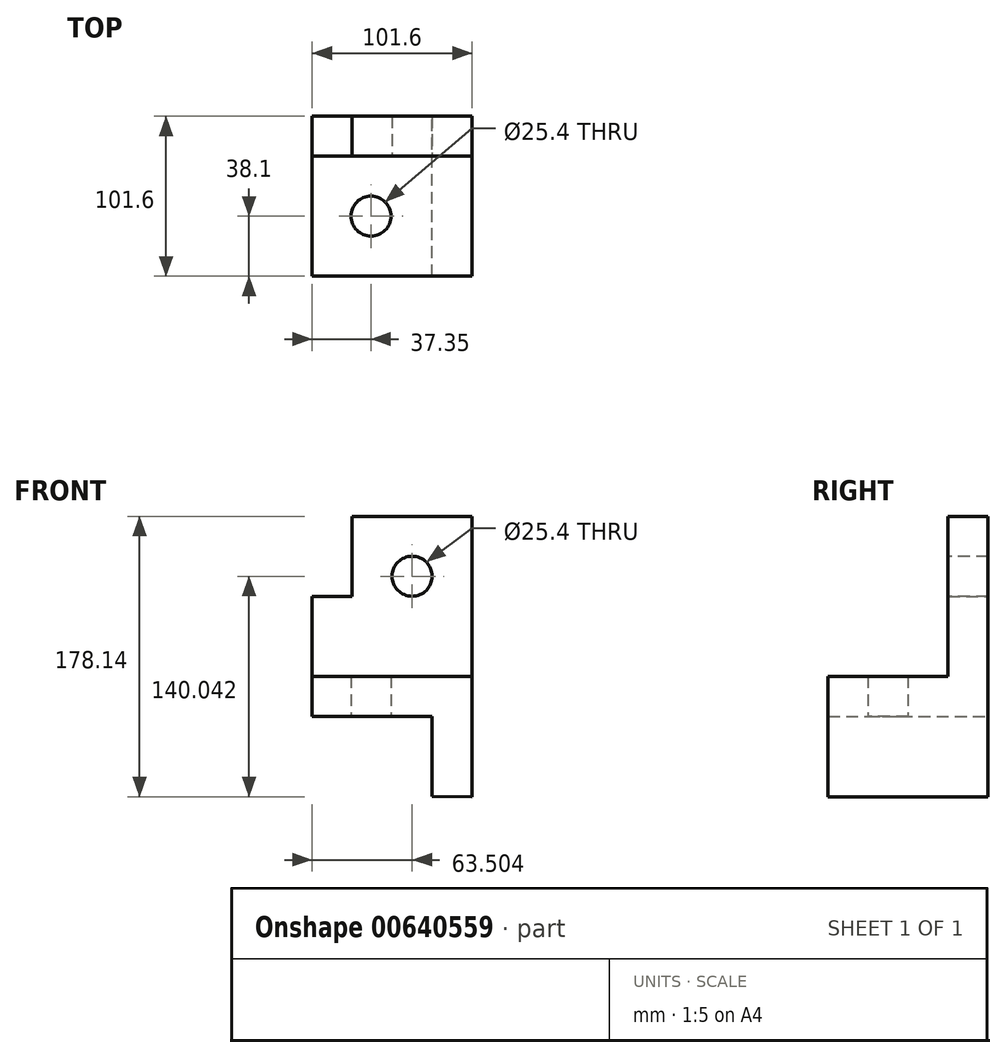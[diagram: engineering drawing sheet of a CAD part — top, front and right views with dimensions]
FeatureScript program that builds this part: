
annotation { "Feature Type Name" : "Feature", "Feature Type Description" : "" }
export const myFeature = defineFeature(function(context is Context, id is Id, definition is map)
    precondition{}
    {
        {
            var Q0;
            Q0=qCreatedBy(makeId("Front.planeOp"),FACE);
            var sketch = newSketch(context, id + "F0", { "sketchPlane" : qUnion([Q0])});
            skLineSegment(sketch, "E0", {"start": v(-11.95, 80.41) * mm, "end": v(64.25, 80.41) * mm});
            skLineSegment(sketch, "E1", {"start": v(64.25, 80.41) * mm, "end": v(64.25, -97.73) * mm});
            skLineSegment(sketch, "E2", {"start": v(-37.35, 29.61) * mm, "end": v(-11.95, 29.61) * mm});
            skLineSegment(sketch, "E3", {"start": v(-11.95, 80.41) * mm, "end": v(-11.95, 29.61) * mm});
            skLineSegment(sketch, "E4", {"start": v(-37.35, -46.59) * mm, "end": v(38.86, -46.59) * mm});
            skLineSegment(sketch, "E5", {"start": v(38.86, -46.59) * mm, "end": v(38.86, -97.39) * mm});
            skLineSegment(sketch, "E6", {"start": v(38.86, -97.39) * mm, "end": v(64.25, -97.73) * mm});
            skPoint(sketch, "E7", {"position": v(-37.35, -46.59) * mm});
            skLineSegment(sketch, "E8", {"start": v(-37.35, 29.61) * mm, "end": v(-37.35, -46.59) * mm});
            skLineSegment(sketch, "E9", {"start": v(-37.35, -21.19) * mm, "end": v(64.25, -21.19) * mm});
            skSolve(sketch);
        }
        {
            var Q0;
            {var subQ2=sQuery(id+"F0.wireOp",EDGE,"E0");Q0=makeQuery(id+"F0.imprint","IMPRINT",FACE,{"disambiguationData":[TD([[makeQuery(id+"F0.imprint","IMPRINT",EDGE,{"derivedFrom":subQ2}),-1.0]])]});}
            extrude(context, id + "F1", {"entities" : qUnion([Q0]), "depth" : 25.4 * mm, "offsetDistance" : 25.4 * mm});
        }
        {
            var Q0;
            {var subQ0=sQuery(id+"F0.wireOp",EDGE,"E4");Q0=makeQuery(id+"F0.imprint","IMPRINT",FACE,{"disambiguationData":[TD([[makeQuery(id+"F0.imprint","IMPRINT",EDGE,{"derivedFrom":subQ0}),1.0]])]});}
            extrude(context, id + "F2", {"entities" : qUnion([Q0]), "operationType" : NewBodyOperationType.ADD, "depth" : 101.6 * mm, "offsetDistance" : 25.4 * mm});
        }
        {
            var Q0;
            Q0=makeQuery(id+"F1.opExtrude","CAP_FACE",FACE,{"disambiguationData":[OSD([sQuery(id+"F0.wireOp",EDGE,"E0"),sQuery(id+"F0.wireOp",EDGE,"E1"),sQuery(id+"F0.wireOp",EDGE,"E2"),sQuery(id+"F0.wireOp",EDGE,"E3"),sQuery(id+"F0.wireOp",EDGE,"E8"),sQuery(id+"F0.wireOp",EDGE,"E9")])],"isStart":false});
            var sketch = newSketch(context, id + "F3", { "sketchPlane" : qUnion([Q0])});
            skCircle(sketch, "E10", {"center": v(26.15, 42.31) * mm, "radius": 12.7 * mm});
            skSolve(sketch);
        }
        {
            var Q0;
            Q0=makeQuery(id+"F3.imprint","IMPRINT",FACE,{"disambiguationData":[TD([[makeQuery(id+"F3.imprint","IMPRINT",EDGE,{"derivedFrom":sQuery(id+"F3.wireOp",EDGE,"E10")}),1.0]])]});
            extrude(context, id + "F4", {"entities" : qUnion([Q0]), "operationType" : NewBodyOperationType.REMOVE, "oppositeDirection" : true, "depth" : 25.4 * mm, "offsetDistance" : 25.4 * mm});
        }
        {
            var Q0;
            Q0=makeQuery(id+"F2.opExtrude","SWEPT_FACE",FACE,{"disambiguationData":[OSD([sQuery(id+"F0.wireOp",EDGE,"E4")])]});
            var sketch = newSketch(context, id + "F5", { "sketchPlane" : qUnion([Q0])});
            skCircle(sketch, "E11", {"center": v(0, 63.5) * mm, "radius": 12.7 * mm});
            skSolve(sketch);
        }
        {
            var Q0;
            Q0=makeQuery(id+"F5.imprint","IMPRINT",FACE,{"disambiguationData":[TD([[makeQuery(id+"F5.imprint","IMPRINT",EDGE,{"derivedFrom":sQuery(id+"F5.wireOp",EDGE,"E11")}),1.0]])]});
            extrude(context, id + "F6", {"entities" : qUnion([Q0]), "operationType" : NewBodyOperationType.REMOVE, "oppositeDirection" : true, "depth" : 25.4 * mm, "offsetDistance" : 25.4 * mm});
        }
    });
